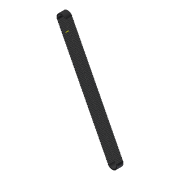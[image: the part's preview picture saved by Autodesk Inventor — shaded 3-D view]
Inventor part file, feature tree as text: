
AUTODESK INVENTOR PART (.ipt)
format: ipt  version: 2012 (Build 160160000, 160)  size: 1,281,536 bytes
history: native  units: in
note: dims shown in document units (in); Inventor stores cm internally (conversion verified against a paired STEP export)
features: extrude x2, sketch x2, pattern_linear x1, plane x1, mirror x1
ambient origin geometry x8: Origin, YZ Plane, XZ Plane, XY Plane, X Axis, Y Axis, Z Axis, Center Point
bodies: Solid1 (feature_tree)
feature tree (7):
  extrude  "Extrusion1"  Depth=0.2in
  extrude  "Extrusion2"  Depth=0.0625in
  pattern_linear  "Rectangular Pattern2"  Spacing1=1.0in  [1 undecoded]
  plane  "Work Plane1"
  mirror  "Mirror1"
  sketch  "Sketch1"  dims[d0=0.625in d1=0.2in]
  sketch  "Sketch3"  dims[d2=1.0in d3=0.0in d5=0.0625in d6=1.0in d7=0.0in d13=35.4331in d15=0.625in]
note: 1 required parameter value undecoded (feature->parameter linkage not recoverable at this tier; creation-order binding heuristic only, values carry confidence <= 0.55)
